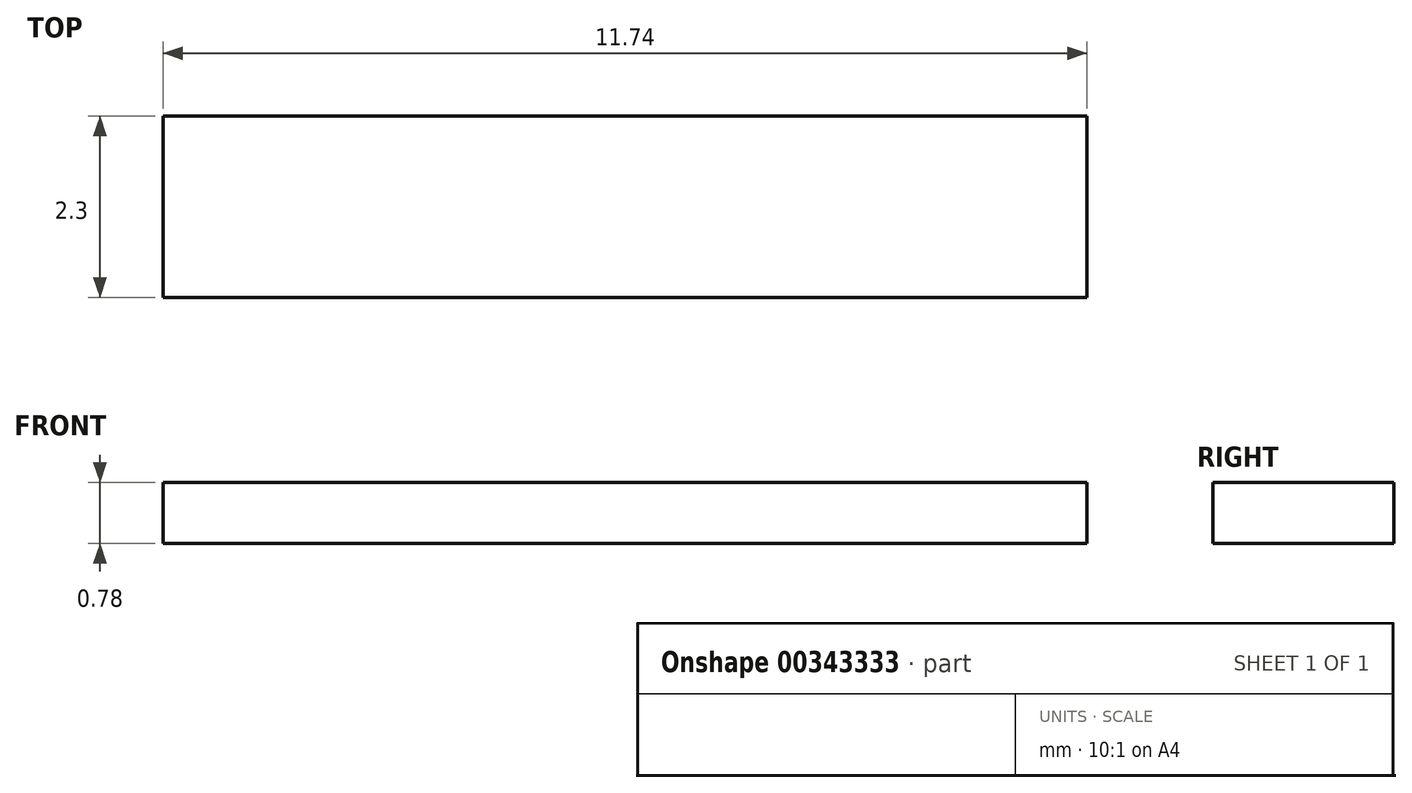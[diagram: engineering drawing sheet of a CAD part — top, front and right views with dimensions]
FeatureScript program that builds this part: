
annotation { "Feature Type Name" : "Feature", "Feature Type Description" : "" }
export const myFeature = defineFeature(function(context is Context, id is Id, definition is map)
    precondition{}
    {
        {
            var Q0;
            Q0=qCreatedBy(makeId("Top.planeOp"),FACE);
            var sketch = newSketch(context, id + "F0", { "sketchPlane" : qUnion([Q0])});
            skLineSegment(sketch, "E0.bottom", {"start": v(-5.87, 1.15) * mm, "end": v(5.87, 1.15) * mm});
            skLineSegment(sketch, "E0.top", {"start": v(-5.87, -1.15) * mm, "end": v(5.87, -1.15) * mm});
            skLineSegment(sketch, "E0.left", {"start": v(-5.87, 1.15) * mm, "end": v(-5.87, -1.15) * mm});
            skLineSegment(sketch, "E0.right", {"start": v(5.87, 1.15) * mm, "end": v(5.87, -1.15) * mm});
            skPoint(sketch, "E0.middle", {"position": v(0, 0) * mm});
            skSolve(sketch);
        }
        {
            var Q0;
            Q0=qSketchRegion(id+"F0",true);
            extrude(context, id + "F1", {"entities" : qUnion([Q0]), "depth" : .780 * mm});
        }
    });
